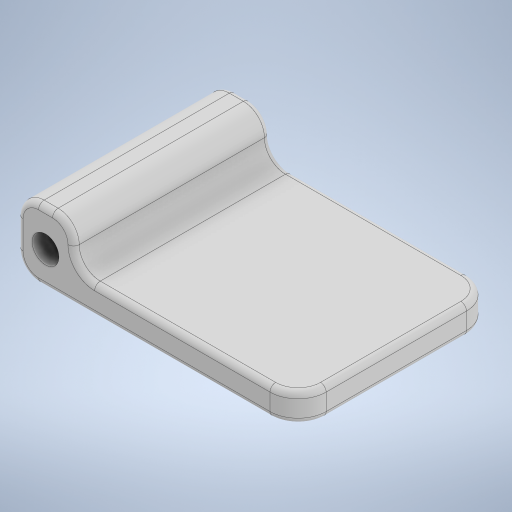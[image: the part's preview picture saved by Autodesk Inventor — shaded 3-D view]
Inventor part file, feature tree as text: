
AUTODESK INVENTOR PART (.ipt)
format: ipt  version: 2023 (Build 270158000, 158)  size: 283,648 bytes
history: native  units: in
note: dims shown in document units (in); Inventor stores cm internally (conversion verified against a paired STEP export)
features: fillet x3, extrude x1, sketch x1
ambient origin geometry x8: Origin, YZ Plane, XZ Plane, XY Plane, X Axis, Y Axis, Z Axis, Center Point
bodies: Solid1 (feature_tree)
feature tree (5):
  extrude  "Extrusion1"  Depth=1.9685in
  fillet  "Fillet1"  Radius=1.5748in
  fillet  "Fillet2"  Radius=0.7874in
  fillet  "Fillet3"  Radius=0.75in
  sketch  "Sketch1"  dims[d0=7.874in d1=1.9685in d2=1.5748in d3=0.7874in d4=0.75in d5=5.5118in d6=0.0in d7=0.5906in d8=0.7874in d9=0.1575in d10=0.0in]
